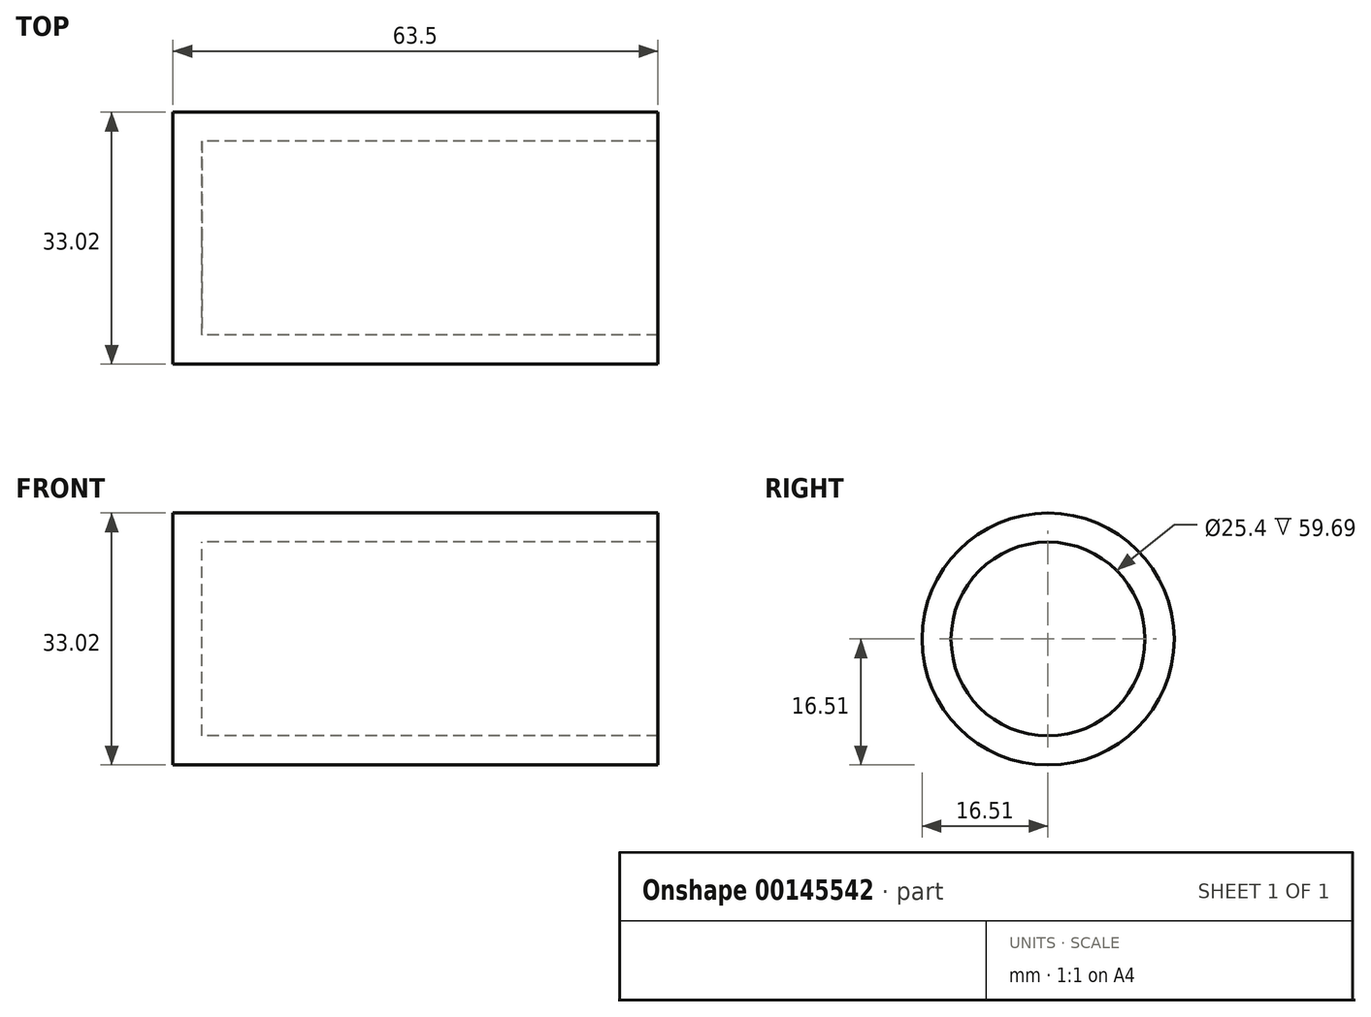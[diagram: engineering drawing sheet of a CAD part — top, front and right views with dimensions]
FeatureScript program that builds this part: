
annotation { "Feature Type Name" : "Feature", "Feature Type Description" : "" }
export const myFeature = defineFeature(function(context is Context, id is Id, definition is map)
    precondition{}
    {
        {
            var Q0;
            Q0=qCreatedBy(makeId("Right.planeOp"),FACE);
            var sketch = newSketch(context, id + "F0", { "sketchPlane" : qUnion([Q0])});
            skCircle(sketch, "E0", {"center": v(0, 0) * mm, "radius": 16.51 * mm});
            skSolve(sketch);
        }
        {
            var Q0;
            Q0=makeQuery(id+"F0.imprint","IMPRINT",FACE,{"disambiguationData":[TD([[makeQuery(id+"F0.imprint","IMPRINT",EDGE,{"derivedFrom":sQuery(id+"F0.wireOp",EDGE,"E0")}),1.0]])]});
            extrude(context, id + "F1", {"entities" : qUnion([Q0]), "depth" : 63.5 * mm});
        }
        {
            var Q0;
            Q0=makeQuery(id+"F1.opExtrude","CAP_FACE",FACE,{"disambiguationData":[OSD([sQuery(id+"F0.wireOp",EDGE,"E0")])],"isStart":false});
            shell(context, id + "F2", {"entities" : qUnion([Q0]), "thickness" : 3.8 * mm});
        }
    });
